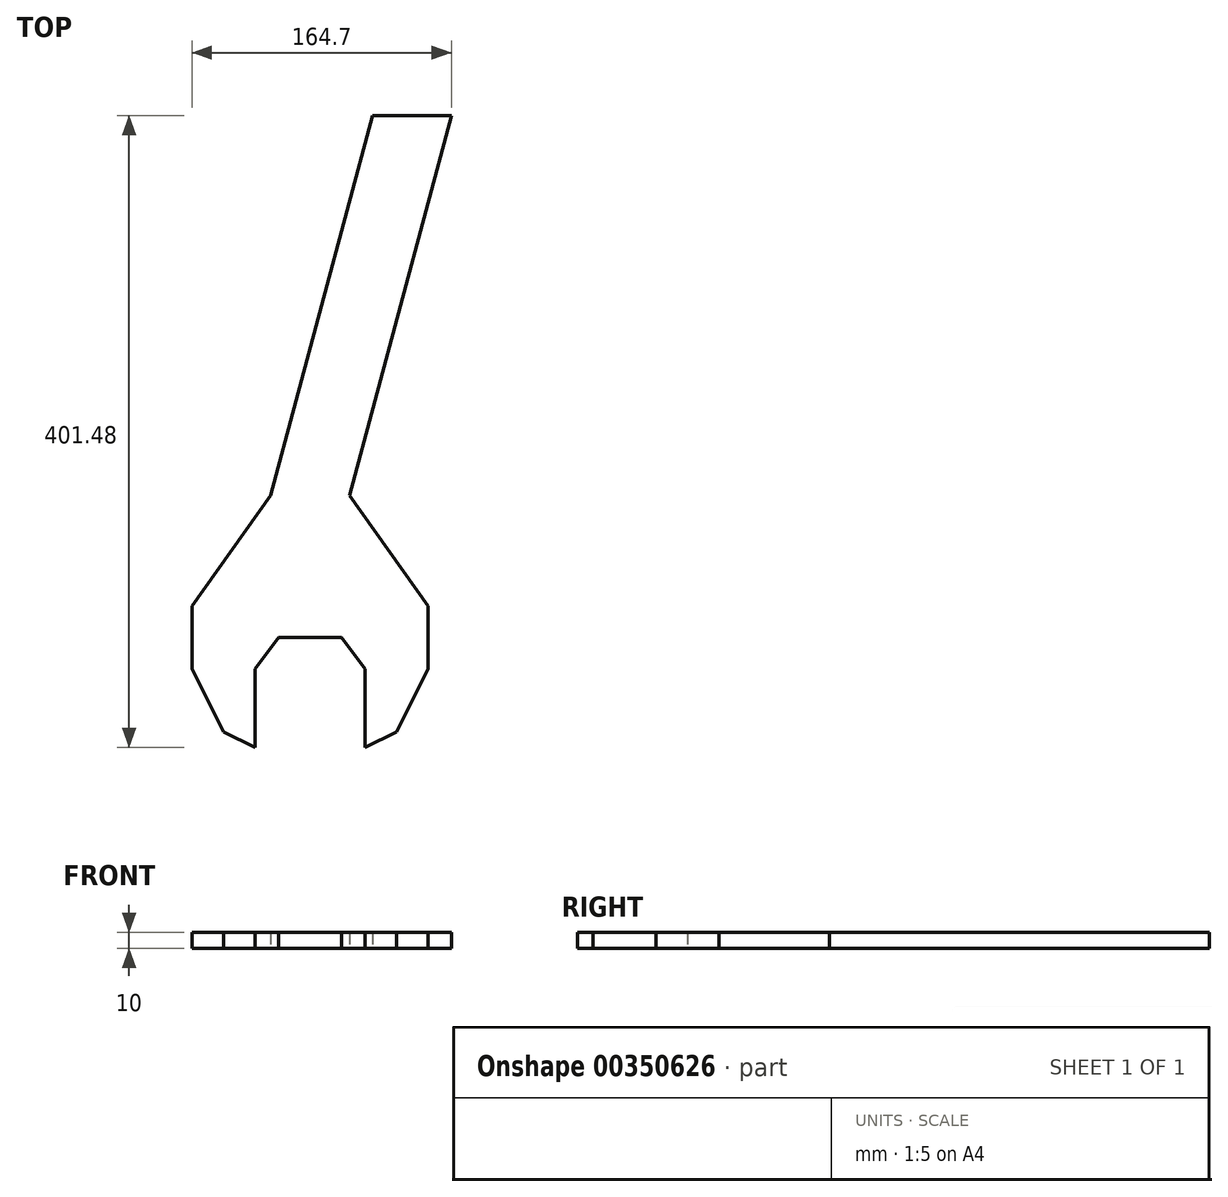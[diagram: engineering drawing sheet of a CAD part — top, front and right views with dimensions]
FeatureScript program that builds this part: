
annotation { "Feature Type Name" : "Feature", "Feature Type Description" : "" }
export const myFeature = defineFeature(function(context is Context, id is Id, definition is map)
    precondition{}
    {
        {
            var Q0;
            Q0=qCreatedBy(makeId("Top.planeOp"),FACE);
            var sketch = newSketch(context, id + "F0", { "sketchPlane" : qUnion([Q0])});
            skLineSegment(sketch, "E0", {"start": v(-20, 0) * mm, "end": v(20, 0) * mm});
            skLineSegment(sketch, "E1", {"start": v(-20, 0) * mm, "end": v(-35, -20) * mm});
            skLineSegment(sketch, "E2", {"start": v(-35, -20) * mm, "end": v(-35, -70) * mm});
            skLineSegment(sketch, "E3", {"start": v(0, 0) * mm, "end": v(0, -67.64) * mm, "construction": true});
            skLineSegment(sketch, "E4.MirrorCS", {"start": v(20, 0) * mm, "end": v(35, -20) * mm});
            skLineSegment(sketch, "E5.MirrorCS", {"start": v(35, -20) * mm, "end": v(35, -70) * mm});
            skLineSegment(sketch, "E6", {"start": v(-35, -70) * mm, "end": v(-55, -60) * mm});
            skLineSegment(sketch, "E7", {"start": v(-55, -60) * mm, "end": v(-75, -20) * mm});
            skLineSegment(sketch, "E8", {"start": v(-75, -20) * mm, "end": v(-75, 20) * mm});
            skLineSegment(sketch, "E9", {"start": v(-75, 20) * mm, "end": v(-25, 90) * mm});
            skLineSegment(sketch, "E10.MirrorCS", {"start": v(35, -70) * mm, "end": v(55, -60) * mm});
            skLineSegment(sketch, "E11.MirrorCS", {"start": v(55, -60) * mm, "end": v(75, -20) * mm});
            skLineSegment(sketch, "E12.MirrorCS", {"start": v(75, 20) * mm, "end": v(25, 90) * mm});
            skLineSegment(sketch, "E13.MirrorCS", {"start": v(75, -20) * mm, "end": v(75, 20) * mm});
            skLineSegment(sketch, "E14", {"start": v(-25, 90) * mm, "end": v(39.7, 331.48) * mm});
            skLineSegment(sketch, "E15", {"start": v(39.7, 331.48) * mm, "end": v(89.7, 331.48) * mm});
            skLineSegment(sketch, "E16", {"start": v(89.7, 331.48) * mm, "end": v(25, 90) * mm});
            skLineSegment(sketch, "E17", {"start": v(25, 90) * mm, "end": v(157.59, 90) * mm, "construction": true});
            skSolve(sketch);
        }
        {
            var Q0;
            Q0=makeQuery(id+"F0.imprint","IMPRINT",FACE,{"disambiguationData":[TD([[makeQuery(id+"F0.imprint","IMPRINT",EDGE,{"derivedFrom":sQuery(id+"F0.wireOp",EDGE,"E0")}),1.0]])]});
            extrude(context, id + "F1", {"entities" : qUnion([Q0]), "depth" : 10 * mm});
        }
    });
